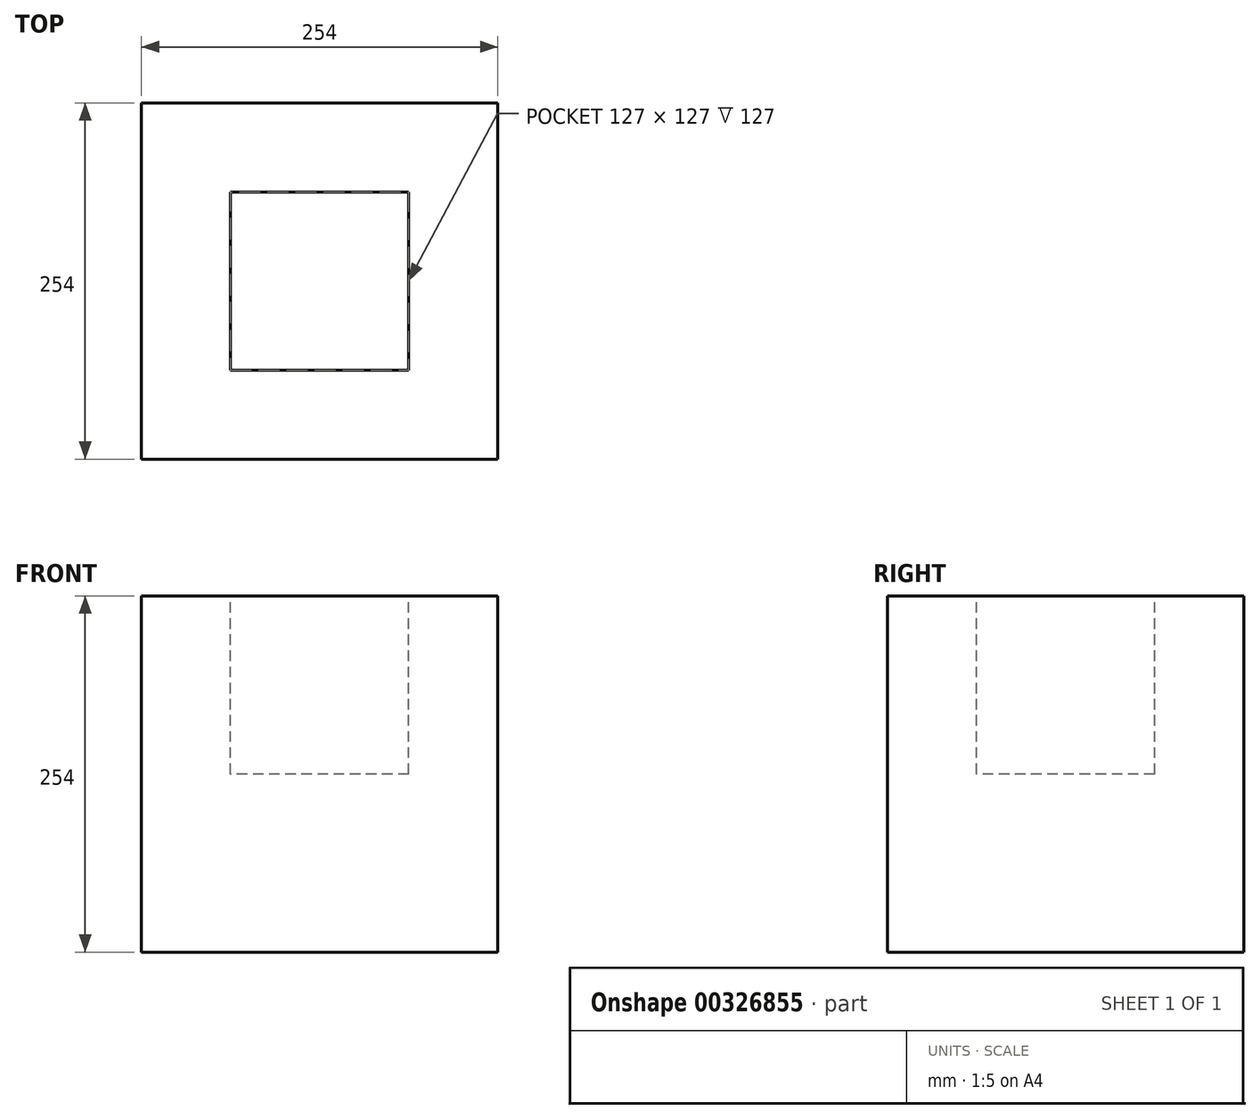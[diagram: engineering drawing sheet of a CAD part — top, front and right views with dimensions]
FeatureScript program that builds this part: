
annotation { "Feature Type Name" : "Feature", "Feature Type Description" : "" }
export const myFeature = defineFeature(function(context is Context, id is Id, definition is map)
    precondition{}
    {
        {
            var Q0;
            Q0=qCreatedBy(makeId("Top.planeOp"),FACE);
            var sketch = newSketch(context, id + "F0", { "sketchPlane" : qUnion([Q0])});
            skLineSegment(sketch, "E0.bottom", {"start": v(0, 0) * mm, "end": v(254, 0) * mm});
            skLineSegment(sketch, "E0.top", {"start": v(0, 254) * mm, "end": v(254, 254) * mm});
            skLineSegment(sketch, "E0.left", {"start": v(0, 0) * mm, "end": v(0, 254) * mm});
            skLineSegment(sketch, "E0.right", {"start": v(254, 0) * mm, "end": v(254, 254) * mm});
            skPoint(sketch, "E0.middle", {"position": v(127, 127) * mm});
            skSolve(sketch);
        }
        {
            var Q0;
            Q0=makeQuery(id+"F0.imprint","IMPRINT",FACE,{"disambiguationData":[TD([[makeQuery(id+"F0.imprint","IMPRINT",EDGE,{"derivedFrom":sQuery(id+"F0.wireOp",EDGE,"E0.bottom")}),1.0]])]});
            extrude(context, id + "F1", {"entities" : qUnion([Q0]), "depth" : 254 * mm});
        }
        {
            var Q0;
            Q0=makeQuery(id+"F1.opExtrude","CAP_FACE",FACE,{"disambiguationData":[OSD([sQuery(id+"F0.wireOp",EDGE,"E0.bottom"),sQuery(id+"F0.wireOp",EDGE,"E0.top"),sQuery(id+"F0.wireOp",EDGE,"E0.left"),sQuery(id+"F0.wireOp",EDGE,"E0.right")])],"isStart":false});
            var sketch = newSketch(context, id + "F2", { "sketchPlane" : qUnion([Q0])});
            skPoint(sketch, "E1", {"position": v(127, 127) * mm});
            skLineSegment(sketch, "E2.bottom", {"start": v(190.5, 190.5) * mm, "end": v(63.5, 190.5) * mm});
            skLineSegment(sketch, "E2.top", {"start": v(190.5, 63.5) * mm, "end": v(63.5, 63.5) * mm});
            skLineSegment(sketch, "E2.left", {"start": v(190.5, 190.5) * mm, "end": v(190.5, 63.5) * mm});
            skLineSegment(sketch, "E2.right", {"start": v(63.5, 190.5) * mm, "end": v(63.5, 63.5) * mm});
            skSolve(sketch);
        }
        {
            var Q0;
            Q0=makeQuery(id+"F2.imprint","IMPRINT",FACE,{"disambiguationData":[TD([[makeQuery(id+"F2.imprint","IMPRINT",EDGE,{"derivedFrom":sQuery(id+"F2.wireOp",EDGE,"E2.bottom")}),1.0]])]});
            extrude(context, id + "F3", {"entities" : qUnion([Q0]), "operationType" : NewBodyOperationType.REMOVE, "oppositeDirection" : true, "depth" : 127 * mm});
        }
    });
